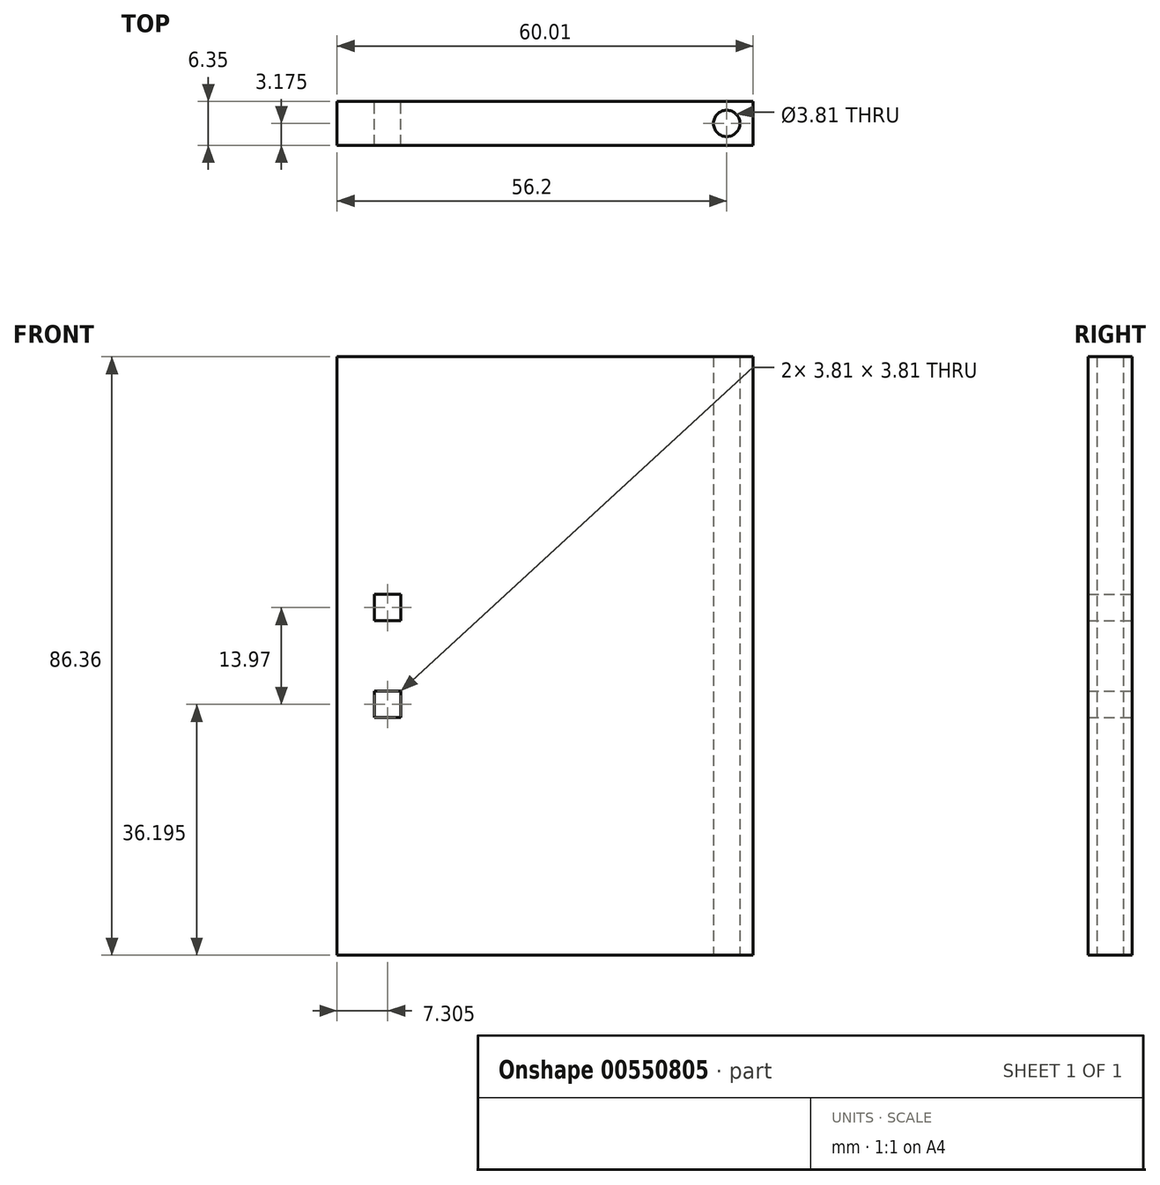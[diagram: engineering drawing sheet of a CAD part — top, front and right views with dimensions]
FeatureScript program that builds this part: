
annotation { "Feature Type Name" : "Feature", "Feature Type Description" : "" }
export const myFeature = defineFeature(function(context is Context, id is Id, definition is map)
    precondition{}
    {
        {
            var Q0;
            Q0=qCreatedBy(makeId("Front.planeOp"),FACE);
            var sketch = newSketch(context, id + "F0", { "sketchPlane" : qUnion([Q0])});
            skLineSegment(sketch, "E0.bottom", {"start": v(0, 0) * mm, "end": v(-60, 0) * mm});
            skLineSegment(sketch, "E0.top", {"start": v(0, 86.36) * mm, "end": v(-60, 86.36) * mm});
            skLineSegment(sketch, "E0.left", {"start": v(0, 0) * mm, "end": v(0, 86.36) * mm});
            skLineSegment(sketch, "E0.right", {"start": v(-60, 0) * mm, "end": v(-60, 86.36) * mm});
            skLineSegment(sketch, "E1.left", {"start": v(-54.61, 52.07) * mm, "end": v(-54.61, 48.26) * mm});
            skLineSegment(sketch, "E1.right", {"start": v(-50.8, 52.07) * mm, "end": v(-50.8, 48.26) * mm});
            skLineSegment(sketch, "E2", {"start": v(-60, 43.18) * mm, "end": v(0, 43.18) * mm, "construction": true});
            skLineSegment(sketch, "E3", {"start": v(-54.61, 48.26) * mm, "end": v(-50.8, 48.26) * mm});
            skLineSegment(sketch, "E4", {"start": v(-54.61, 52.07) * mm, "end": v(-50.8, 52.07) * mm});
            skLineSegment(sketch, "E5.MirrorCS", {"start": v(-54.61, 38.1) * mm, "end": v(-50.8, 38.1) * mm});
            skLineSegment(sketch, "E6.MirrorCS", {"start": v(-54.6, 34.29) * mm, "end": v(-54.61, 38.1) * mm});
            skLineSegment(sketch, "E7.MirrorCS", {"start": v(-54.6, 34.29) * mm, "end": v(-50.8, 34.29) * mm});
            skLineSegment(sketch, "E8.MirrorCS", {"start": v(-50.8, 34.29) * mm, "end": v(-50.8, 38.1) * mm});
            skSolve(sketch);
        }
        {
            var Q0;
            Q0=makeQuery(id+"F0.imprint","IMPRINT",FACE,{"disambiguationData":[TD([[makeQuery(id+"F0.imprint","IMPRINT",EDGE,{"derivedFrom":sQuery(id+"F0.wireOp",EDGE,"E0.bottom")}),-1.0]])]});
            extrude(context, id + "F1", {"entities" : qUnion([Q0]), "depth" : 6.35 * mm, "offsetDistance" : 25.4 * mm});
        }
        {
            var Q0;
            Q0=qCreatedBy(makeId("Top.planeOp"),FACE);
            var sketch = newSketch(context, id + "F2", { "sketchPlane" : qUnion([Q0])});
            skCircle(sketch, "E9", {"center": v(-3.81, -3.18) * mm, "radius": 1.9 * mm});
            skSolve(sketch);
        }
        {
            var Q0;
            Q0=makeQuery(id+"F2.imprint","IMPRINT",FACE,{"disambiguationData":[TD([[makeQuery(id+"F2.imprint","IMPRINT",EDGE,{"derivedFrom":sQuery(id+"F2.wireOp",EDGE,"E9")}),1.0]])]});
            var Q1;
            Q1=sQuery(id+"F2.wireOp",EDGE,"E9");
            extrude(context, id + "F3", {"entities" : qUnion([Q0]), "operationType" : NewBodyOperationType.REMOVE, "surfaceEntities" : qUnion([Q1]), "endBound" : BoundingType.THROUGH_ALL, "depth" : 25.4 * mm, "offsetDistance" : 25.4 * mm});
        }
    });
